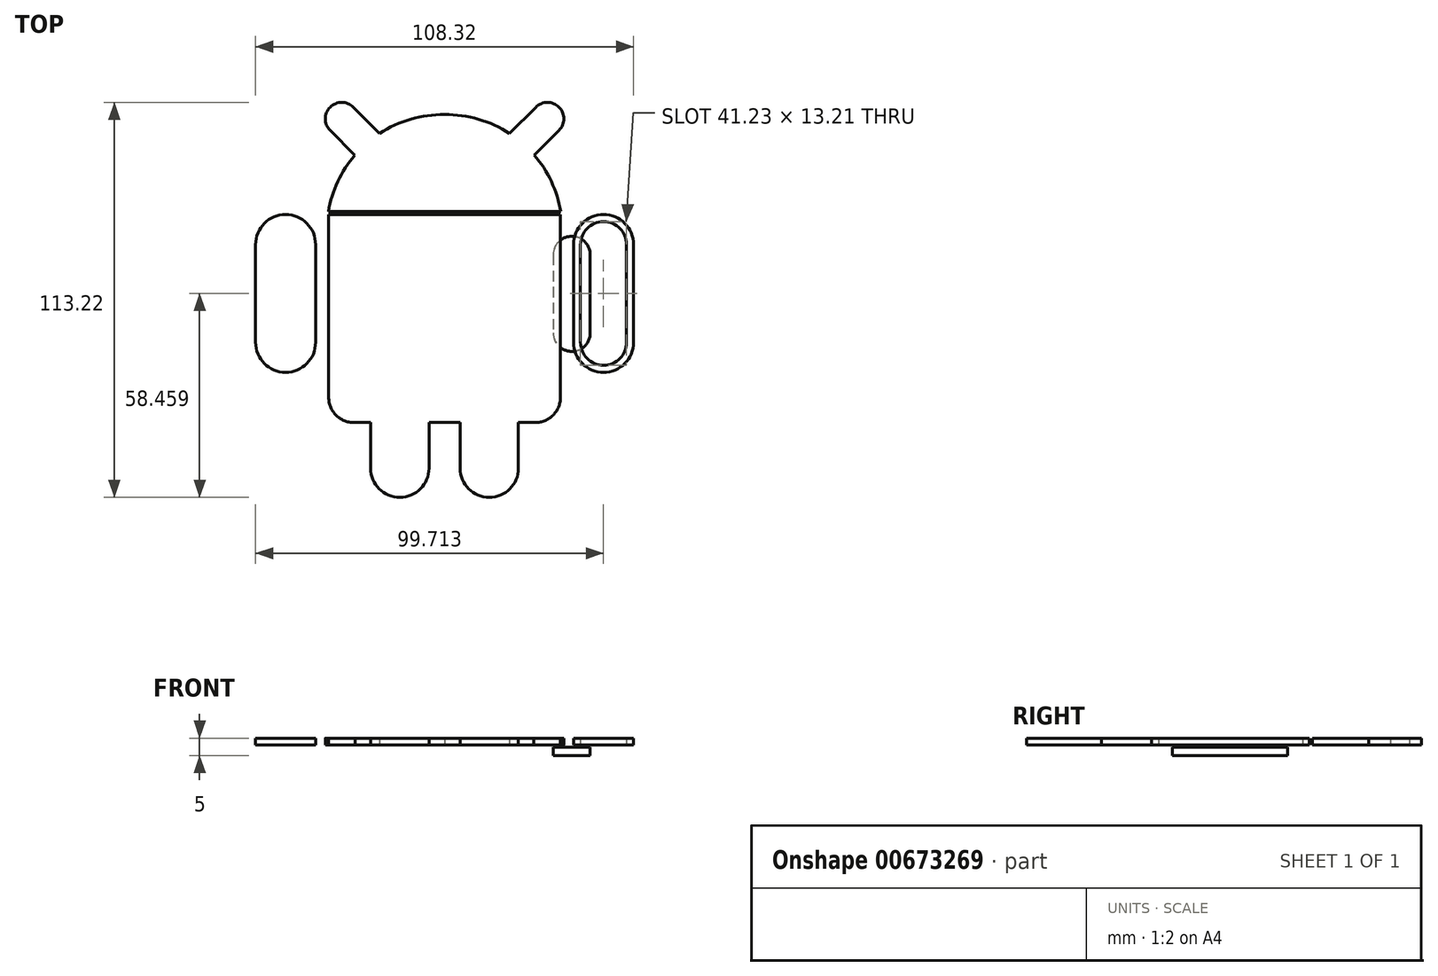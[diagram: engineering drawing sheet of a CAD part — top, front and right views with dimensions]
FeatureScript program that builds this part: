
annotation { "Feature Type Name" : "Feature", "Feature Type Description" : "" }
export const myFeature = defineFeature(function(context is Context, id is Id, definition is map)
    precondition{}
    {
        {
            var Q0;
            Q0=qCreatedBy(makeId("Top.planeOp"),FACE);
            var sketch = newSketch(context, id + "F0", { "sketchPlane" : qUnion([Q0])});
            skCircle(sketch, "E0", {"center": v(0, 0) * mm, "radius": 69.53 * mm});
            skLineSegment(sketch, "E1", {"start": v(-7.31, 69.15) * mm, "end": v(-7.31, 87.88) * mm});
            skPoint(sketch, "E2", {"position": v(0, 69.53) * mm});
            skArc(sketch, "E3", {"start": v(-7.31, 87.88) * mm, "mid": v(-5.17, 93.06) * mm, "end": v(0, 95.2) * mm});
            skLineSegment(sketch, "E4.MirrorCS", {"start": v(7.31, 69.15) * mm, "end": v(7.31, 87.88) * mm});
            skArc(sketch, "E5.MirrorCS", {"start": v(7.31, 87.88) * mm, "mid": v(5.17, 93.06) * mm, "end": v(0, 95.2) * mm});
            skLineSegment(sketch, "E6.1.0", {"start": v(-69.15, -7.31) * mm, "end": v(-87.88, -7.31) * mm});
            skArc(sketch, "E6.1.1", {"start": v(-87.88, -7.31) * mm, "mid": v(-93.06, -5.17) * mm, "end": v(-95.2, 0) * mm});
            skArc(sketch, "E6.1.2", {"start": v(-87.88, 7.31) * mm, "mid": v(-93.06, 5.17) * mm, "end": v(-95.2, 0) * mm});
            skLineSegment(sketch, "E6.1.3", {"start": v(-69.15, 7.31) * mm, "end": v(-87.88, 7.31) * mm});
            skLineSegment(sketch, "E6.2.0", {"start": v(7.31, -69.15) * mm, "end": v(7.31, -87.88) * mm});
            skArc(sketch, "E6.2.1", {"start": v(7.31, -87.88) * mm, "mid": v(5.17, -93.06) * mm, "end": v(0, -95.2) * mm});
            skArc(sketch, "E6.2.2", {"start": v(-7.31, -87.88) * mm, "mid": v(-5.17, -93.06) * mm, "end": v(0, -95.2) * mm});
            skLineSegment(sketch, "E6.2.3", {"start": v(-7.31, -69.15) * mm, "end": v(-7.31, -87.88) * mm});
            skLineSegment(sketch, "E6.3.0", {"start": v(69.15, 7.31) * mm, "end": v(87.88, 7.31) * mm});
            skArc(sketch, "E6.3.1", {"start": v(87.88, 7.31) * mm, "mid": v(93.06, 5.17) * mm, "end": v(95.2, 0) * mm});
            skArc(sketch, "E6.3.2", {"start": v(87.88, -7.31) * mm, "mid": v(93.06, -5.17) * mm, "end": v(95.2, 0) * mm});
            skLineSegment(sketch, "E6.3.3", {"start": v(69.15, -7.31) * mm, "end": v(87.88, -7.31) * mm});
            skSolve(sketch);
        }
        {
            var Q0;
            Q0 = qSketchRegion(id + "F0", true);
            extrude(context, id + "F1", {"entities" : qUnion([Q0]), "depth" : 3 * mm, "offsetDistance" : 25 * mm});
        }
        {
            var Q0;
            Q0=makeQuery(id+"F1.opExtrude","CAP_FACE",FACE,{"disambiguationData":[OSD([sQuery(id+"F0.wireOp",EDGE,"E0")])],"isStart":false});
            var sketch = newSketch(context, id + "F2", { "sketchPlane" : qUnion([Q0])});
            skLineSegment(sketch, "E7", {"start": v(-31.2, 21.21) * mm, "end": v(0, 21.21) * mm});
            skLineSegment(sketch, "E8", {"start": v(-31.2, 21.21) * mm, "end": v(-31.2, -29.16) * mm});
            skArc(sketch, "E9", {"start": v(-31.2, -29.16) * mm, "mid": v(-29.55, -32.97) * mm, "end": v(-25.64, -34.37) * mm});
            skLineSegment(sketch, "E10", {"start": v(-25.64, -34.37) * mm, "end": v(-19.17, -34.37) * mm});
            skLineSegment(sketch, "E11", {"start": v(-19.17, -34.37) * mm, "end": v(-19.17, -49.49) * mm});
            skArc(sketch, "E12", {"start": v(-19.17, -49.49) * mm, "mid": v(-12.82, -55.84) * mm, "end": v(-6.47, -49.49) * mm});
            skLineSegment(sketch, "E13", {"start": v(-6.47, -49.49) * mm, "end": v(-6.47, -34.37) * mm});
            skLineSegment(sketch, "E14", {"start": v(-6.47, -34.37) * mm, "end": v(0, -34.37) * mm});
            skLineSegment(sketch, "E15", {"start": v(0, 0) * mm, "end": v(0, 63.34) * mm, "construction": true});
            skPoint(sketch, "E16", {"position": v(0, 21.21) * mm});
            skLineSegment(sketch, "E17", {"start": v(-19.17, -34.37) * mm, "end": v(-6.47, -34.37) * mm, "construction": true});
            skArc(sketch, "E18", {"start": v(0, 50.19) * mm, "mid": v(-9.88, 48.74) * mm, "end": v(-18.82, 44.28) * mm});
            skPoint(sketch, "E18.first.point", {"position": v(-31.2, 25.8) * mm});
            skPoint(sketch, "E18.second.point", {"position": v(0, 50.19) * mm});
            skLineSegment(sketch, "E19", {"start": v(0, 21.21) * mm, "end": v(-31.59, 52.8) * mm, "construction": true});
            skLineSegment(sketch, "E20", {"start": v(-23.36, 40.32) * mm, "end": v(-31.59, 48.55) * mm});
            skLineSegment(sketch, "E21", {"start": v(-31.59, 48.55) * mm, "end": v(-27.34, 52.8) * mm, "construction": true});
            skLineSegment(sketch, "E22", {"start": v(-27.34, 52.8) * mm, "end": v(-18.82, 44.28) * mm});
            skArc(sketch, "E23", {"start": v(-27.34, 52.8) * mm, "mid": v(-31.59, 52.8) * mm, "end": v(-31.59, 48.55) * mm});
            skArc(sketch, "E24", {"start": v(-18.82, 44.28) * mm, "mid": v(-21.19, 42.41) * mm, "end": v(-23.36, 40.32) * mm, "construction": true});
            skArc(sketch, "E25", {"start": v(-23.36, 40.32) * mm, "mid": v(-24.04, 39.6) * mm, "end": v(-24.69, 38.84) * mm});
            skLineSegment(sketch, "E26.bottom", {"start": v(-52.16, 14.63) * mm, "end": v(-38.95, 14.63) * mm, "construction": true});
            skLineSegment(sketch, "E26.top", {"start": v(-52.16, -13.4) * mm, "end": v(-38.95, -13.4) * mm, "construction": true});
            skLineSegment(sketch, "E26.left", {"start": v(-52.16, 14.63) * mm, "end": v(-52.16, -13.4) * mm});
            skLineSegment(sketch, "E26.right", {"start": v(-38.95, 14.63) * mm, "end": v(-38.95, -13.4) * mm});
            skArc(sketch, "E27", {"start": v(-38.95, 14.63) * mm, "mid": v(-45.55, 21.23) * mm, "end": v(-52.16, 14.63) * mm});
            skArc(sketch, "E28", {"start": v(-52.16, -13.4) * mm, "mid": v(-45.55, -20) * mm, "end": v(-38.95, -13.4) * mm});
            skPoint(sketch, "E29", {"position": v(-45.55, 21.23) * mm});
            skPoint(sketch, "E30.first.point", {"position": v(-9.61, 37.46) * mm});
            skPoint(sketch, "E30.second.point", {"position": v(-13.05, 40.8) * mm});
            skPoint(sketch, "E30.third.point", {"position": v(-15.18, 34.95) * mm});
            skLineSegment(sketch, "E31", {"start": v(-9.61, 37.46) * mm, "end": v(-25.78, 37.46) * mm, "construction": true});
            skLineSegment(sketch, "E32", {"start": v(-16.01, 38.84) * mm, "end": v(-24.69, 38.84) * mm});
            skLineSegment(sketch, "E33.MirrorCS", {"start": v(-16.01, 36.07) * mm, "end": v(-26.75, 36.07) * mm});
            skPoint(sketch, "E34.orphan", {"position": v(-24.69, 36.07) * mm});
            skArc(sketch, "E35", {"start": v(-24.69, 38.84) * mm, "mid": v(-25.76, 37.48) * mm, "end": v(-26.75, 36.07) * mm, "construction": true});
            skArc(sketch, "E36", {"start": v(-26.75, 36.07) * mm, "mid": v(-29.44, 31.13) * mm, "end": v(-31.2, 25.8) * mm});
            skArc(sketch, "E37", {"start": v(-16.01, 38.84) * mm, "mid": v(-16.3, 37.46) * mm, "end": v(-16.01, 36.07) * mm, "construction": true});
            skArc(sketch, "E38", {"start": v(-16.01, 36.07) * mm, "mid": v(-9.61, 37.46) * mm, "end": v(-16.01, 38.84) * mm});
            skLineSegment(sketch, "E39", {"start": v(-31.2, 25.8) * mm, "end": v(0, 25.8) * mm});
            skArc(sketch, "E40.MirrorCS", {"start": v(0, 50.19) * mm, "mid": v(9.88, 48.74) * mm, "end": v(18.82, 44.28) * mm});
            skLineSegment(sketch, "E41.MirrorCS", {"start": v(27.34, 52.8) * mm, "end": v(18.82, 44.28) * mm});
            skArc(sketch, "E42.MirrorCS", {"start": v(16.01, 38.84) * mm, "mid": v(16.3, 37.46) * mm, "end": v(16.01, 36.07) * mm, "construction": true});
            skArc(sketch, "E43.MirrorCS", {"start": v(23.36, 40.32) * mm, "mid": v(24.04, 39.6) * mm, "end": v(24.69, 38.84) * mm});
            skArc(sketch, "E44.MirrorCS", {"start": v(24.69, 38.84) * mm, "mid": v(25.76, 37.48) * mm, "end": v(26.75, 36.07) * mm, "construction": true});
            skLineSegment(sketch, "E45.MirrorCS", {"start": v(6.47, -34.37) * mm, "end": v(0, -34.37) * mm});
            skLineSegment(sketch, "E46.MirrorCS", {"start": v(31.59, 48.55) * mm, "end": v(27.34, 52.8) * mm, "construction": true});
            skPoint(sketch, "E47.MirrorP", {"position": v(13.05, 40.8) * mm});
            skArc(sketch, "E48.MirrorCS", {"start": v(26.75, 36.07) * mm, "mid": v(29.44, 31.13) * mm, "end": v(31.2, 25.8) * mm});
            skLineSegment(sketch, "E49.MirrorCS", {"start": v(16.01, 36.07) * mm, "end": v(26.75, 36.07) * mm});
            skPoint(sketch, "E50.MirrorP", {"position": v(24.69, 36.07) * mm});
            skArc(sketch, "E51.MirrorCS", {"start": v(52.16, -13.4) * mm, "mid": v(45.55, -20) * mm, "end": v(38.95, -13.4) * mm});
            skLineSegment(sketch, "E52.MirrorCS", {"start": v(52.16, 14.63) * mm, "end": v(52.16, -13.4) * mm});
            skLineSegment(sketch, "E53.MirrorCS", {"start": v(23.36, 40.32) * mm, "end": v(31.59, 48.55) * mm});
            skPoint(sketch, "E54.MirrorP", {"position": v(9.61, 37.46) * mm});
            skArc(sketch, "E55.MirrorCS", {"start": v(27.34, 52.8) * mm, "mid": v(31.59, 52.8) * mm, "end": v(31.59, 48.55) * mm});
            skArc(sketch, "E56.MirrorCS", {"start": v(19.17, -49.49) * mm, "mid": v(12.82, -55.84) * mm, "end": v(6.47, -49.49) * mm});
            skLineSegment(sketch, "E57.MirrorCS", {"start": v(25.64, -34.37) * mm, "end": v(19.17, -34.37) * mm});
            skLineSegment(sketch, "E58.MirrorCS", {"start": v(31.2, 21.21) * mm, "end": v(0, 21.21) * mm});
            skLineSegment(sketch, "E59.MirrorCS", {"start": v(38.95, 14.63) * mm, "end": v(38.95, -13.4) * mm});
            skLineSegment(sketch, "E60.MirrorCS", {"start": v(6.47, -49.49) * mm, "end": v(6.47, -34.37) * mm});
            skLineSegment(sketch, "E61.MirrorCS", {"start": v(19.17, -34.37) * mm, "end": v(6.47, -34.37) * mm, "construction": true});
            skLineSegment(sketch, "E62.MirrorCS", {"start": v(52.16, 14.63) * mm, "end": v(38.95, 14.63) * mm, "construction": true});
            skPoint(sketch, "E63.MirrorP", {"position": v(15.18, 34.95) * mm});
            skPoint(sketch, "E64.MirrorP", {"position": v(31.2, 25.8) * mm});
            skArc(sketch, "E65.MirrorCS", {"start": v(16.01, 36.07) * mm, "mid": v(9.61, 37.46) * mm, "end": v(16.01, 38.84) * mm});
            skLineSegment(sketch, "E66.MirrorCS", {"start": v(9.61, 37.46) * mm, "end": v(25.78, 37.46) * mm, "construction": true});
            skLineSegment(sketch, "E67.MirrorCS", {"start": v(19.17, -34.37) * mm, "end": v(19.17, -49.49) * mm});
            skArc(sketch, "E68.MirrorCS", {"start": v(38.95, 14.63) * mm, "mid": v(45.55, 21.23) * mm, "end": v(52.16, 14.63) * mm});
            skPoint(sketch, "E69.MirrorP", {"position": v(45.55, 21.23) * mm});
            skArc(sketch, "E70.MirrorCS", {"start": v(31.2, -29.16) * mm, "mid": v(29.55, -32.97) * mm, "end": v(25.64, -34.37) * mm});
            skLineSegment(sketch, "E71.MirrorCS", {"start": v(16.01, 38.84) * mm, "end": v(24.69, 38.84) * mm});
            skArc(sketch, "E72.MirrorCS", {"start": v(18.82, 44.28) * mm, "mid": v(21.19, 42.41) * mm, "end": v(23.36, 40.32) * mm, "construction": true});
            skLineSegment(sketch, "E73.MirrorCS", {"start": v(0, 21.21) * mm, "end": v(31.59, 52.8) * mm, "construction": true});
            skLineSegment(sketch, "E74.MirrorCS", {"start": v(52.16, -13.4) * mm, "end": v(38.95, -13.4) * mm, "construction": true});
            skLineSegment(sketch, "E75.MirrorCS", {"start": v(31.2, 21.21) * mm, "end": v(31.2, -29.16) * mm});
            skLineSegment(sketch, "E76.MirrorCS", {"start": v(31.2, 25.8) * mm, "end": v(0, 25.8) * mm});
            skSolve(sketch);
        }
        {
            var Q0;
            Q0=makeQuery(id+"F2.imprint","IMPRINT",FACE,{"disambiguationData":[TD([[makeQuery(id+"F2.imprint","IMPRINT",EDGE,{"derivedFrom":sQuery(id+"F2.wireOp",EDGE,"E26.left")}),1.0]])]});
            var Q1;
            Q1=makeQuery(id+"F2.imprint","IMPRINT",FACE,{"disambiguationData":[TD([[makeQuery(id+"F2.imprint","IMPRINT",EDGE,{"derivedFrom":sQuery(id+"F2.wireOp",EDGE,"E7")}),-1.0]])]});
            var Q2;
            Q2=makeQuery(id+"F2.imprint","IMPRINT",FACE,{"disambiguationData":[TD([[makeQuery(id+"F2.imprint","IMPRINT",EDGE,{"derivedFrom":sQuery(id+"F2.wireOp",EDGE,"E51.MirrorCS")}),-1.0]])]});
            var Q3;
            Q3=makeQuery(id+"F2.imprint","IMPRINT",FACE,{"disambiguationData":[TD([[makeQuery(id+"F2.imprint","IMPRINT",EDGE,{"derivedFrom":sQuery(id+"F2.wireOp",EDGE,"E18")}),1.0]])]});
            extrude(context, id + "F3", {"entities" : qUnion([Q0, Q1, Q2, Q3]), "operationType" : NewBodyOperationType.REMOVE, "oppositeDirection" : true, "depth" : 25 * mm, "offsetDistance" : 25 * mm});
        }
        {
            var Q0;
            Q0=makeQuery(id+"F1.opExtrude","CAP_FACE",FACE,{"disambiguationData":[OSD([sQuery(id+"F0.wireOp",EDGE,"E0")])],"isStart":false});
            var sketch = newSketch(context, id + "F4", { "sketchPlane" : qUnion([Q0])});
            skArc(sketch, "E77.0", {"start": v(-36.95, 14.63) * mm, "mid": v(-45.55, 23.23) * mm, "end": v(-54.16, 14.63) * mm});
            skLineSegment(sketch, "E77.1", {"start": v(-36.95, 14.63) * mm, "end": v(-36.95, -13.4) * mm});
            skArc(sketch, "E77.2", {"start": v(-54.16, -13.4) * mm, "mid": v(-45.55, -22) * mm, "end": v(-36.95, -13.4) * mm});
            skLineSegment(sketch, "E77.3", {"start": v(-54.16, 14.63) * mm, "end": v(-54.16, -13.4) * mm});
            skLineSegment(sketch, "E78.0", {"start": v(33.2, 23.21) * mm, "end": v(-33.2, 23.21) * mm});
            skLineSegment(sketch, "E78.1", {"start": v(33.2, 23.21) * mm, "end": v(33.2, -29.16) * mm});
            skArc(sketch, "E78.2", {"start": v(33.2, -29.16) * mm, "mid": v(30.95, -34.4) * mm, "end": v(25.58, -36.37) * mm});
            skArc(sketch, "E78.3", {"start": v(-21.17, -49.49) * mm, "mid": v(-12.82, -57.84) * mm, "end": v(-4.47, -49.49) * mm});
            skLineSegment(sketch, "E78.4", {"start": v(-21.17, -36.37) * mm, "end": v(-21.17, -49.49) * mm});
            skLineSegment(sketch, "E78.5", {"start": v(-25.58, -36.37) * mm, "end": v(-21.17, -36.37) * mm});
            skArc(sketch, "E78.6", {"start": v(-33.2, -29.16) * mm, "mid": v(-30.95, -34.4) * mm, "end": v(-25.58, -36.37) * mm});
            skLineSegment(sketch, "E78.7", {"start": v(-4.47, -49.49) * mm, "end": v(-4.47, -36.37) * mm});
            skLineSegment(sketch, "E78.8", {"start": v(-4.47, -36.37) * mm, "end": v(4.47, -36.37) * mm});
            skLineSegment(sketch, "E78.9", {"start": v(4.47, -49.49) * mm, "end": v(4.47, -36.37) * mm});
            skLineSegment(sketch, "E78.10", {"start": v(-33.2, 23.21) * mm, "end": v(-33.2, -29.16) * mm});
            skArc(sketch, "E78.11", {"start": v(21.17, -49.49) * mm, "mid": v(12.82, -57.84) * mm, "end": v(4.47, -49.49) * mm});
            skLineSegment(sketch, "E78.12", {"start": v(21.17, -36.37) * mm, "end": v(21.17, -49.49) * mm});
            skLineSegment(sketch, "E78.13", {"start": v(25.58, -36.37) * mm, "end": v(21.17, -36.37) * mm});
            skArc(sketch, "E79.0", {"start": v(-30.7, 32.46) * mm, "mid": v(-32.27, 28.36) * mm, "end": v(-33.28, 24.1) * mm});
            skArc(sketch, "E79.1", {"start": v(-25.7, 40.26) * mm, "mid": v(-28.48, 36.54) * mm, "end": v(-30.7, 32.46) * mm});
            skArc(sketch, "E79.2", {"start": v(26.14, 54) * mm, "mid": v(32.8, 54) * mm, "end": v(32.8, 47.35) * mm});
            skLineSegment(sketch, "E79.3", {"start": v(25.7, 40.26) * mm, "end": v(32.8, 47.35) * mm});
            skArc(sketch, "E79.4", {"start": v(25.7, 40.26) * mm, "mid": v(28.48, 36.54) * mm, "end": v(30.7, 32.46) * mm});
            skArc(sketch, "E79.5", {"start": v(30.7, 32.46) * mm, "mid": v(32.27, 28.36) * mm, "end": v(33.28, 24.1) * mm});
            skLineSegment(sketch, "E79.6", {"start": v(26.14, 54) * mm, "end": v(18.61, 46.48) * mm});
            skArc(sketch, "E79.7", {"start": v(0, 51.89) * mm, "mid": v(9.7, 50.57) * mm, "end": v(18.61, 46.48) * mm});
            skLineSegment(sketch, "E79.8", {"start": v(-33.28, 24.1) * mm, "end": v(33.28, 24.1) * mm});
            skArc(sketch, "E79.9", {"start": v(0, 51.89) * mm, "mid": v(-9.7, 50.57) * mm, "end": v(-18.61, 46.48) * mm});
            skLineSegment(sketch, "E79.10", {"start": v(-26.14, 54) * mm, "end": v(-18.61, 46.48) * mm});
            skArc(sketch, "E79.11", {"start": v(-26.14, 54) * mm, "mid": v(-32.8, 54) * mm, "end": v(-32.8, 47.35) * mm});
            skLineSegment(sketch, "E79.12", {"start": v(-25.7, 40.26) * mm, "end": v(-32.8, 47.35) * mm});
            skLineSegment(sketch, "E80.0", {"start": v(36.95, 14.63) * mm, "end": v(36.95, -13.4) * mm});
            skArc(sketch, "E80.1", {"start": v(36.95, 14.63) * mm, "mid": v(45.55, 23.23) * mm, "end": v(54.16, 14.63) * mm});
            skLineSegment(sketch, "E80.2", {"start": v(54.16, 14.63) * mm, "end": v(54.16, -13.4) * mm});
            skArc(sketch, "E80.3", {"start": v(54.16, -13.4) * mm, "mid": v(45.55, -22) * mm, "end": v(36.95, -13.4) * mm});
            skLineSegment(sketch, "E81", {"start": v(-33.2, 23.21) * mm, "end": v(-33.2, 27.37) * mm, "construction": true});
            skSolve(sketch);
        }
        {
            var Q0;
            Q0=makeQuery(id+"F4.imprint","IMPRINT",FACE,{"disambiguationData":[TD([[makeQuery(id+"F4.imprint","IMPRINT",EDGE,{"derivedFrom":sQuery(id+"F4.wireOp",EDGE,"E77.0")}),1.0]])]});
            var Q1;
            Q1=makeQuery(id+"F4.imprint","IMPRINT",FACE,{"disambiguationData":[TD([[makeQuery(id+"F4.imprint","IMPRINT",EDGE,{"derivedFrom":sQuery(id+"F4.wireOp",EDGE,"E78.0")}),1.0]])]});
            var Q2;
            Q2=makeQuery(id+"F4.imprint","IMPRINT",FACE,{"disambiguationData":[TD([[makeQuery(id+"F4.imprint","IMPRINT",EDGE,{"derivedFrom":sQuery(id+"F4.wireOp",EDGE,"E80.0")}),1.0]])]});
            var Q3;
            Q3=makeQuery(id+"F4.imprint","IMPRINT",FACE,{"disambiguationData":[TD([[makeQuery(id+"F4.imprint","IMPRINT",EDGE,{"derivedFrom":sQuery(id+"F4.wireOp",EDGE,"E79.0")}),1.0]])]});
            extrude(context, id + "F5", {"entities" : qUnion([Q0, Q1, Q2, Q3]), "operationType" : NewBodyOperationType.ADD, "depth" : 2 * mm, "offsetDistance" : 25 * mm});
        }
        {
            var Q0;
            Q0=makeQuery(id+"F1.opExtrude","SWEPT_BODY",BODY,{"disambiguationData":[OSD([sQuery(id+"F0.wireOp",EDGE,"E0")])]});
            var Q1;
            Q1=qCreatedBy(makeId("Origin.pointOp"),VERTEX);
            transform(context, id + "F6", {"entities" : qUnion([Q0]), "transformType" : TransformType.SCALE_UNIFORMLY, "scale" : 0.8, "scalePoint" : qUnion([Q1]), "makeCopy" : false});
        }
    });
